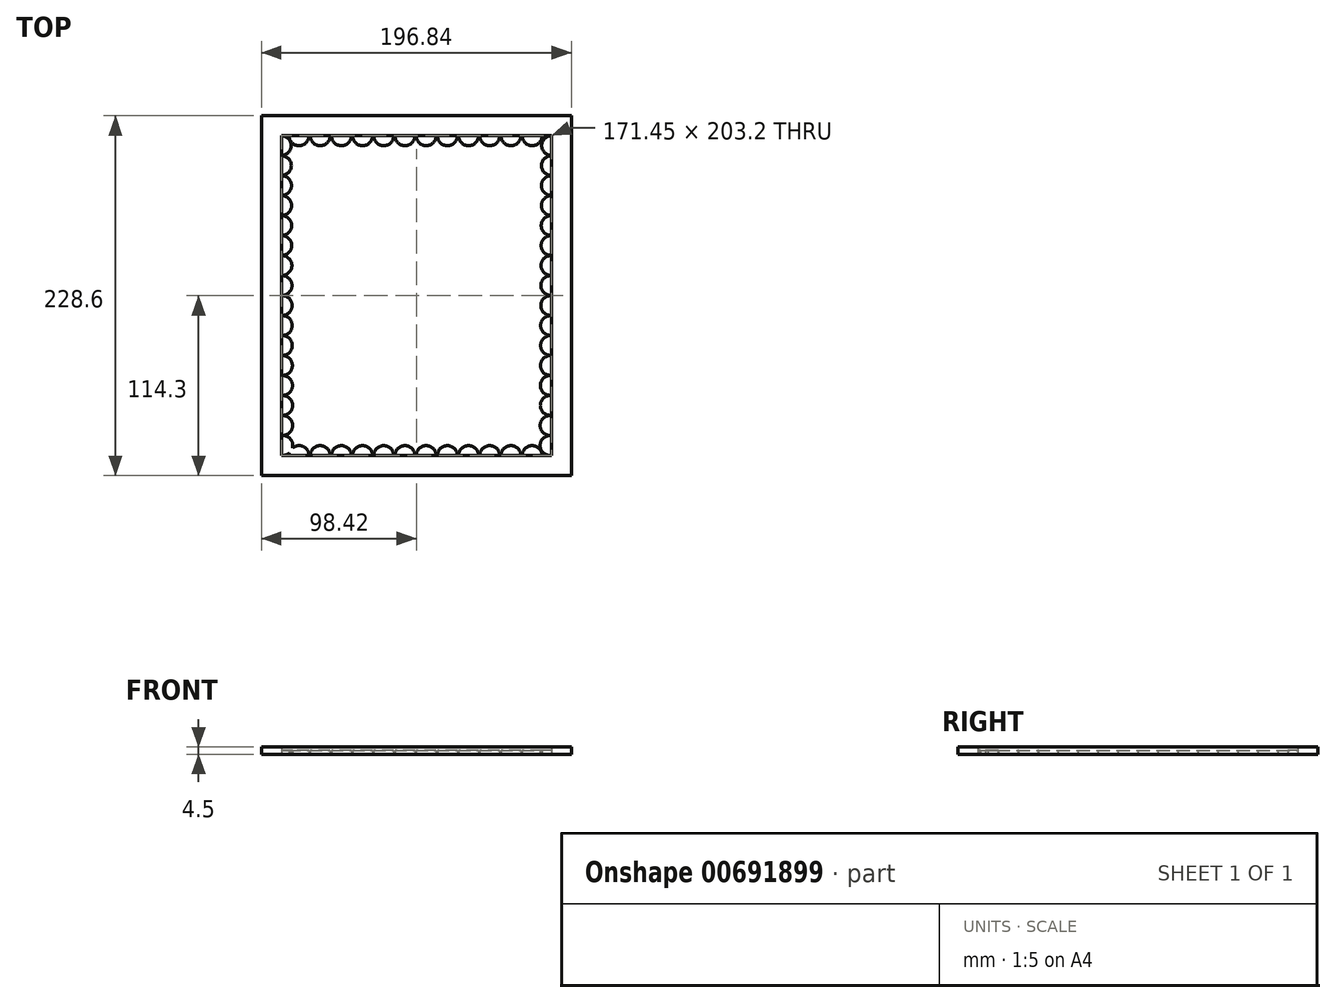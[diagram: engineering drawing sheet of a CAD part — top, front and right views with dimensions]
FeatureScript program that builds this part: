
annotation { "Feature Type Name" : "Feature", "Feature Type Description" : "" }
export const myFeature = defineFeature(function(context is Context, id is Id, definition is map)
    precondition{}
    {
        {
            var Q0;
            Q0=qCreatedBy(makeId("Top.planeOp"),FACE);
            var sketch = newSketch(context, id + "F0", { "sketchPlane" : qUnion([Q0])});
            skLineSegment(sketch, "E0.bottom", {"start": v(-98.42, 114.3) * mm, "end": v(98.43, 114.3) * mm});
            skLineSegment(sketch, "E0.top", {"start": v(-98.43, -114.3) * mm, "end": v(98.43, -114.3) * mm});
            skLineSegment(sketch, "E0.left", {"start": v(-98.42, 114.3) * mm, "end": v(-98.43, -114.3) * mm});
            skLineSegment(sketch, "E0.right", {"start": v(98.43, 114.3) * mm, "end": v(98.43, -114.3) * mm});
            skLineSegment(sketch, "E1.bottom", {"start": v(85.72, -101.6) * mm, "end": v(-85.72, -101.6) * mm});
            skLineSegment(sketch, "E1.top", {"start": v(85.72, 101.6) * mm, "end": v(-85.72, 101.6) * mm});
            skLineSegment(sketch, "E1.left", {"start": v(85.72, -101.6) * mm, "end": v(85.73, 101.6) * mm});
            skLineSegment(sketch, "E1.right", {"start": v(-85.73, -101.6) * mm, "end": v(-85.72, 101.6) * mm});
            skSolve(sketch);
        }
        {
            var Q0;
            Q0=makeQuery(id+"F0.imprint","IMPRINT",FACE,{"disambiguationData":[TD([[makeQuery(id+"F0.imprint","IMPRINT",EDGE,{"derivedFrom":sQuery(id+"F0.wireOp",EDGE,"E1.bottom")}),-1.0]])]});
            var Q1;
            Q1=makeQuery(id+"F0.imprint","IMPRINT",FACE,{"disambiguationData":[TD([[makeQuery(id+"F0.imprint","IMPRINT",EDGE,{"derivedFrom":sQuery(id+"F0.wireOp",EDGE,"E0.bottom")}),-1.0]])]});
            var Q2;
            Q2=sQuery(id+"F0.wireOp",EDGE,"E0.bottom");
            var Q3;
            Q3=sQuery(id+"F0.wireOp",EDGE,"E0.left");
            var Q4;
            Q4=sQuery(id+"F0.wireOp",EDGE,"E0.right");
            var Q5;
            Q5=sQuery(id+"F0.wireOp",EDGE,"E0.top");
            extrude(context, id + "F1", {"entities" : qUnion([Q0, Q1]), "surfaceEntities" : qUnion([Q2, Q3, Q4, Q5]), "depth" : 4.5 * mm, "offsetDistance" : 25.4 * mm});
        }
        {
            var Q0;
            Q0=makeQuery(id+"F0.imprint","IMPRINT",FACE,{"disambiguationData":[TD([[makeQuery(id+"F0.imprint","IMPRINT",EDGE,{"derivedFrom":sQuery(id+"F0.wireOp",EDGE,"E1.bottom")}),-1.0]])]});
            extrude(context, id + "F2", {"entities" : qUnion([Q0]), "operationType" : NewBodyOperationType.REMOVE, "depth" : 4.5 * mm, "offsetDistance" : 25.4 * mm});
        }
        {
            var Q0;
            Q0=makeQuery(id+"F0.imprint","IMPRINT",FACE,{"disambiguationData":[TD([[makeQuery(id+"F0.imprint","IMPRINT",EDGE,{"derivedFrom":sQuery(id+"F0.wireOp",EDGE,"E1.bottom")}),-1.0]])]});
            var sketch = newSketch(context, id + "F3", { "sketchPlane" : qUnion([Q0])});
            skCircle(sketch, "E2", {"center": v(-85.8, 95.31) * mm, "radius": 6.29 * mm});
            skCircle(sketch, "E3.MirrorC", {"center": v(85.8, 95.31) * mm, "radius": 6.29 * mm});
            skCircle(sketch, "E4.0.1.0", {"center": v(-85.73, 82.61) * mm, "radius": 6.29 * mm});
            skCircle(sketch, "E4.0.2.0", {"center": v(-85.66, 69.91) * mm, "radius": 6.29 * mm});
            skCircle(sketch, "E4.0.3.0", {"center": v(-85.6, 57.21) * mm, "radius": 6.29 * mm});
            skCircle(sketch, "E4.0.4.0", {"center": v(-85.53, 44.51) * mm, "radius": 6.29 * mm});
            skCircle(sketch, "E4.0.5.0", {"center": v(-85.46, 31.81) * mm, "radius": 6.29 * mm});
            skCircle(sketch, "E4.0.6.0", {"center": v(-85.4, 19.11) * mm, "radius": 6.29 * mm});
            skCircle(sketch, "E4.0.7.0", {"center": v(-85.33, 6.42) * mm, "radius": 6.29 * mm});
            skCircle(sketch, "E4.0.8.0", {"center": v(-85.27, -6.28) * mm, "radius": 6.29 * mm});
            skCircle(sketch, "E4.0.9.0", {"center": v(-85.2, -18.98) * mm, "radius": 6.29 * mm});
            skCircle(sketch, "E4.0.10.0", {"center": v(-85.14, -31.68) * mm, "radius": 6.29 * mm});
            skCircle(sketch, "E4.0.11.0", {"center": v(-85.07, -44.38) * mm, "radius": 6.29 * mm});
            skCircle(sketch, "E4.0.12.0", {"center": v(-85, -57.08) * mm, "radius": 6.29 * mm});
            skCircle(sketch, "E4.0.13.0", {"center": v(-84.94, -69.78) * mm, "radius": 6.29 * mm});
            skCircle(sketch, "E4.0.14.0", {"center": v(-84.87, -82.48) * mm, "radius": 6.29 * mm});
            skCircle(sketch, "E4.0.15.0", {"center": v(-84.8, -95.18) * mm, "radius": 6.29 * mm});
            skLineSegment(sketch, "E4.direction1", {"start": v(-85.8, 95.31) * mm, "end": v(-60.4, 95.31) * mm, "construction": true});
            skLineSegment(sketch, "E4.direction2", {"start": v(-85.8, 95.31) * mm, "end": v(-85.73, 82.61) * mm, "construction": true});
            skCircle(sketch, "E5.MirrorC", {"center": v(85.73, 82.61) * mm, "radius": 6.29 * mm});
            skCircle(sketch, "E6.MirrorC", {"center": v(85.66, 69.91) * mm, "radius": 6.29 * mm});
            skCircle(sketch, "E7.MirrorC", {"center": v(85.6, 57.21) * mm, "radius": 6.29 * mm});
            skCircle(sketch, "E8.MirrorC", {"center": v(85.53, 44.51) * mm, "radius": 6.29 * mm});
            skCircle(sketch, "E9.MirrorC", {"center": v(85.46, 31.81) * mm, "radius": 6.29 * mm});
            skCircle(sketch, "E10.MirrorC", {"center": v(85.4, 19.11) * mm, "radius": 6.29 * mm});
            skCircle(sketch, "E11.MirrorC", {"center": v(85.33, 6.42) * mm, "radius": 6.29 * mm});
            skCircle(sketch, "E12.MirrorC", {"center": v(85.27, -6.28) * mm, "radius": 6.29 * mm});
            skCircle(sketch, "E13.MirrorC", {"center": v(85.2, -18.98) * mm, "radius": 6.29 * mm});
            skCircle(sketch, "E14.MirrorC", {"center": v(85.14, -31.68) * mm, "radius": 6.29 * mm});
            skCircle(sketch, "E15.MirrorC", {"center": v(85.07, -44.38) * mm, "radius": 6.29 * mm});
            skCircle(sketch, "E16.MirrorC", {"center": v(85, -57.08) * mm, "radius": 6.29 * mm});
            skCircle(sketch, "E17.MirrorC", {"center": v(84.94, -69.78) * mm, "radius": 6.29 * mm});
            skCircle(sketch, "E18.MirrorC", {"center": v(84.87, -82.48) * mm, "radius": 6.29 * mm});
            skCircle(sketch, "E19.MirrorC", {"center": v(84.8, -95.18) * mm, "radius": 6.29 * mm});
            skSolve(sketch);
        }
        {
            var Q0;
            Q0 = qSketchRegion(id + "F3", true);
            extrude(context, id + "F4", {"entities" : qUnion([Q0]), "operationType" : NewBodyOperationType.ADD, "depth" : 2.3 * mm, "offsetDistance" : 25.4 * mm});
        }
        {
            var Q0;
            Q0=makeQuery(id+"F0.imprint","IMPRINT",FACE,{"disambiguationData":[TD([[makeQuery(id+"F0.imprint","IMPRINT",EDGE,{"derivedFrom":sQuery(id+"F0.wireOp",EDGE,"E1.bottom")}),-1.0]])]});
            var sketch = newSketch(context, id + "F5", { "sketchPlane" : qUnion([Q0])});
            skCircle(sketch, "E20", {"center": v(-74.6, 101.6) * mm, "radius": 6.35 * mm});
            skCircle(sketch, "E21.1.0.0", {"center": v(-61.14, 101.6) * mm, "radius": 6.35 * mm});
            skCircle(sketch, "E21.2.0.0", {"center": v(-47.68, 101.6) * mm, "radius": 6.35 * mm});
            skCircle(sketch, "E21.3.0.0", {"center": v(-34.22, 101.6) * mm, "radius": 6.35 * mm});
            skCircle(sketch, "E21.4.0.0", {"center": v(-20.76, 101.6) * mm, "radius": 6.35 * mm});
            skCircle(sketch, "E21.5.0.0", {"center": v(-7.3, 101.6) * mm, "radius": 6.35 * mm});
            skCircle(sketch, "E21.6.0.0", {"center": v(6.17, 101.6) * mm, "radius": 6.35 * mm});
            skCircle(sketch, "E21.7.0.0", {"center": v(19.63, 101.6) * mm, "radius": 6.35 * mm});
            skCircle(sketch, "E21.8.0.0", {"center": v(33.1, 101.6) * mm, "radius": 6.35 * mm});
            skCircle(sketch, "E21.9.0.0", {"center": v(46.55, 101.6) * mm, "radius": 6.35 * mm});
            skCircle(sketch, "E21.10.0.0", {"center": v(60.02, 101.6) * mm, "radius": 6.35 * mm});
            skCircle(sketch, "E21.11.0.0", {"center": v(73.48, 101.6) * mm, "radius": 6.35 * mm});
            skLineSegment(sketch, "E21.direction1", {"start": v(-74.6, 101.6) * mm, "end": v(-61.14, 101.6) * mm, "construction": true});
            skCircle(sketch, "E22.MirrorC", {"center": v(-74.6, -101.6) * mm, "radius": 6.35 * mm});
            skCircle(sketch, "E23.MirrorC", {"center": v(-61.14, -101.6) * mm, "radius": 6.35 * mm});
            skCircle(sketch, "E24.MirrorC", {"center": v(-47.68, -101.6) * mm, "radius": 6.35 * mm});
            skCircle(sketch, "E25.MirrorC", {"center": v(-34.22, -101.6) * mm, "radius": 6.35 * mm});
            skCircle(sketch, "E26.MirrorC", {"center": v(-20.76, -101.6) * mm, "radius": 6.35 * mm});
            skCircle(sketch, "E27.MirrorC", {"center": v(-7.3, -101.6) * mm, "radius": 6.35 * mm});
            skCircle(sketch, "E28.MirrorC", {"center": v(6.17, -101.6) * mm, "radius": 6.35 * mm});
            skCircle(sketch, "E29.MirrorC", {"center": v(19.63, -101.6) * mm, "radius": 6.35 * mm});
            skCircle(sketch, "E30.MirrorC", {"center": v(73.48, -101.6) * mm, "radius": 6.35 * mm});
            skCircle(sketch, "E31.MirrorC", {"center": v(46.55, -101.6) * mm, "radius": 6.35 * mm});
            skCircle(sketch, "E32.MirrorC", {"center": v(33.1, -101.6) * mm, "radius": 6.35 * mm});
            skCircle(sketch, "E33.MirrorC", {"center": v(60.02, -101.6) * mm, "radius": 6.35 * mm});
            skSolve(sketch);
        }
        {
            var Q0;
            Q0 = qSketchRegion(id + "F5", true);
            extrude(context, id + "F6", {"entities" : qUnion([Q0]), "operationType" : NewBodyOperationType.ADD, "depth" : 2.3 * mm, "offsetDistance" : 25.4 * mm});
        }
    });
